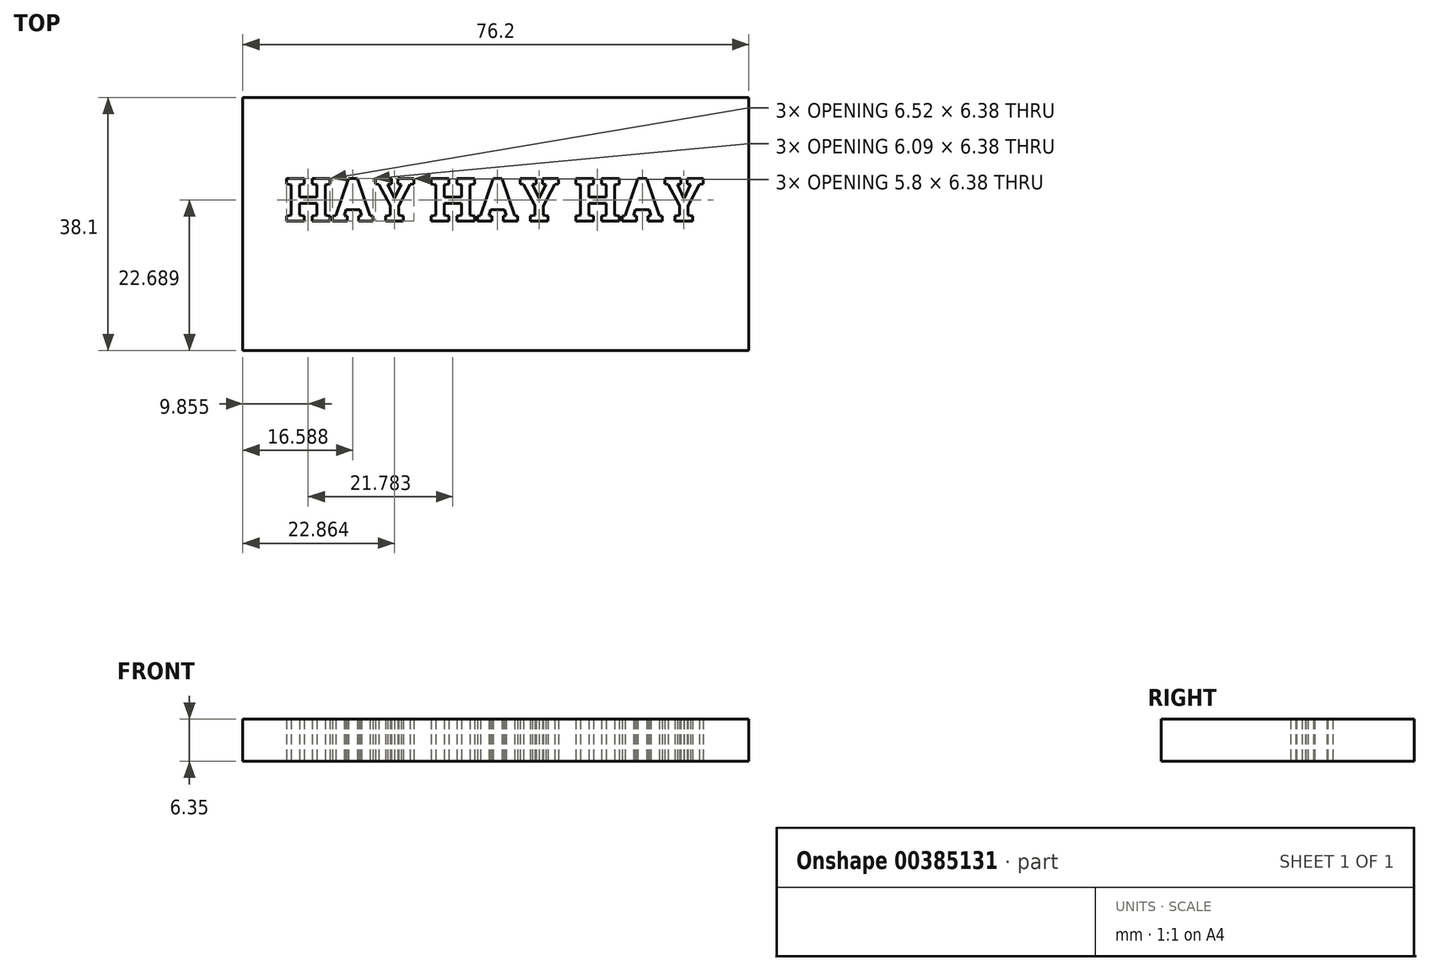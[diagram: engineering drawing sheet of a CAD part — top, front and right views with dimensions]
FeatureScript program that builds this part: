
annotation { "Feature Type Name" : "Feature", "Feature Type Description" : "" }
export const myFeature = defineFeature(function(context is Context, id is Id, definition is map)
    precondition{}
    {
        {
            var Q0;
            Q0=qCreatedBy(makeId("Top.planeOp"),FACE);
            var sketch = newSketch(context, id + "F0", { "sketchPlane" : qUnion([Q0])});
            skLineSegment(sketch, "E0.bottom", {"start": v(-38.1, 19.05) * mm, "end": v(38.1, 19.05) * mm});
            skLineSegment(sketch, "E0.top", {"start": v(-38.1, -19.05) * mm, "end": v(38.1, -19.05) * mm});
            skLineSegment(sketch, "E0.left", {"start": v(-38.1, 19.05) * mm, "end": v(-38.1, -19.05) * mm});
            skLineSegment(sketch, "E0.right", {"start": v(38.1, 19.05) * mm, "end": v(38.1, -19.05) * mm});
            skText(sketch, "E1", { "text": "HAY HAY HAY\n", "fontName": "RobotoSlab-Bold.ttf"});
            const initialGuessF0  = {"E1": [-0.03175, 0.00045, 1, 0, 0.00646]};
            skSetInitialGuess(sketch, initialGuessF0);
            skSolve(sketch);
        }
        {
            var Q0;
            Q0=makeQuery(id+"F0.imprint","IMPRINT",FACE,{"disambiguationData":[TD([[makeQuery(id+"F0.imprint","IMPRINT",EDGE,{"derivedFrom":sQuery(id+"F0.wireOp",EDGE,"E0.bottom")}),-1.0]])]});
            extrude(context, id + "F1", {"entities" : qUnion([Q0]), "depth" : 6.35 * mm});
        }
    });
